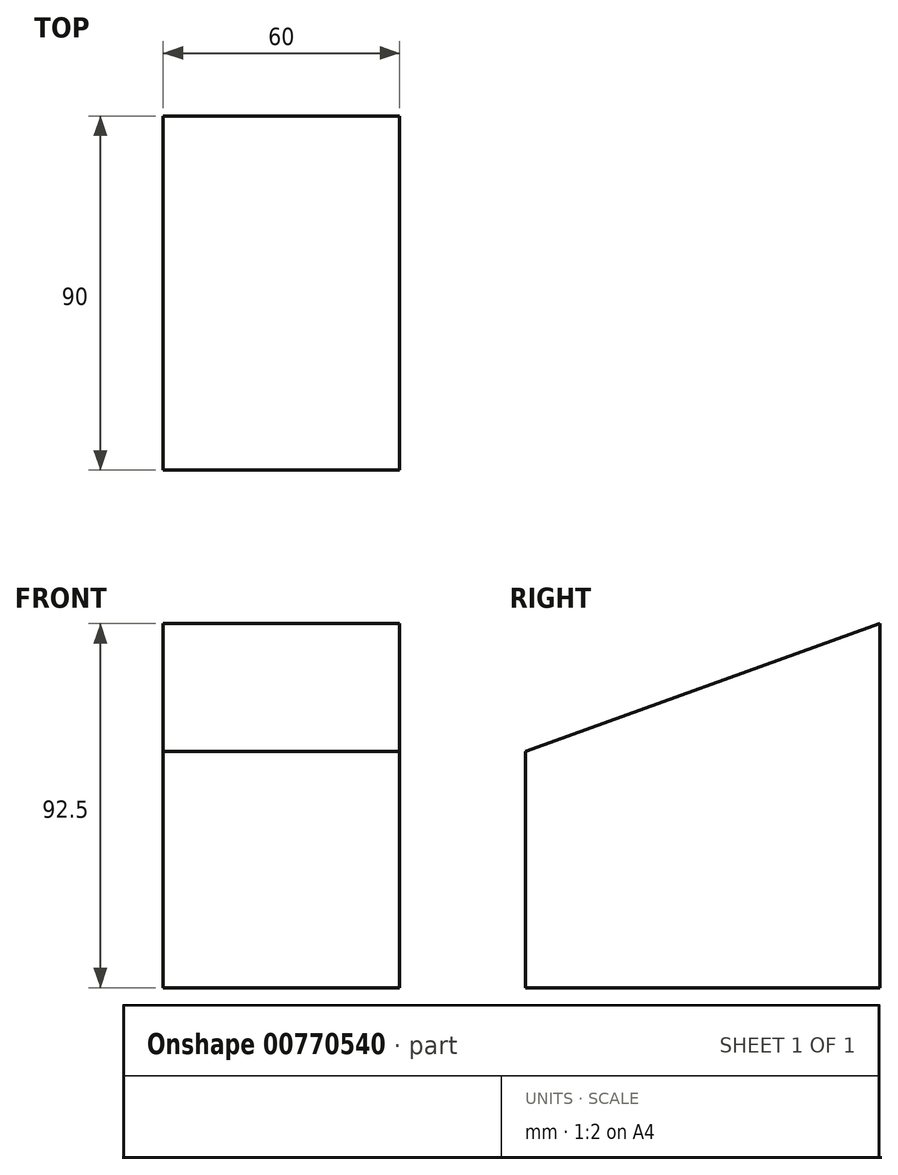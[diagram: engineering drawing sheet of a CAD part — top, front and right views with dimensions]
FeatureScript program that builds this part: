
annotation { "Feature Type Name" : "Feature", "Feature Type Description" : "" }
export const myFeature = defineFeature(function(context is Context, id is Id, definition is map)
    precondition{}
    {
        {
            var Q0;
            Q0=qCreatedBy(makeId("Right.planeOp"),FACE);
            var sketch = newSketch(context, id + "F0", { "sketchPlane" : qUnion([Q0])});
            skLineSegment(sketch, "E0.top", {"start": v(-75.47, -62.53) * mm, "end": v(14.53, -62.53) * mm});
            skPoint(sketch, "E0.middle", {"position": v(0, 0) * mm});
            skLineSegment(sketch, "E1", {"start": v(-75.47, -62.53) * mm, "end": v(-75.47, -2.53) * mm});
            skLineSegment(sketch, "E2", {"start": v(-75.47, -2.53) * mm, "end": v(-75.47, -62.53) * mm});
            skLineSegment(sketch, "E3", {"start": v(14.53, -62.53) * mm, "end": v(14.53, 29.97) * mm});
            skLineSegment(sketch, "E4", {"start": v(14.53, 29.97) * mm, "end": v(-75.47, -2.53) * mm});
            skSolve(sketch);
        }
        {
            var Q0;
            Q0=makeQuery(id+"F0.imprint","IMPRINT",FACE,{"disambiguationData":[TD([[makeQuery(id+"F0.imprint","IMPRINT",EDGE,{"derivedFrom":sQuery(id+"F0.wireOp",EDGE,"E0.top")}),1.0]])]});
            extrude(context, id + "F1", {"entities" : qUnion([Q0]), "depth" : 60 * mm, "offsetDistance" : 25.4 * mm});
        }
    });
